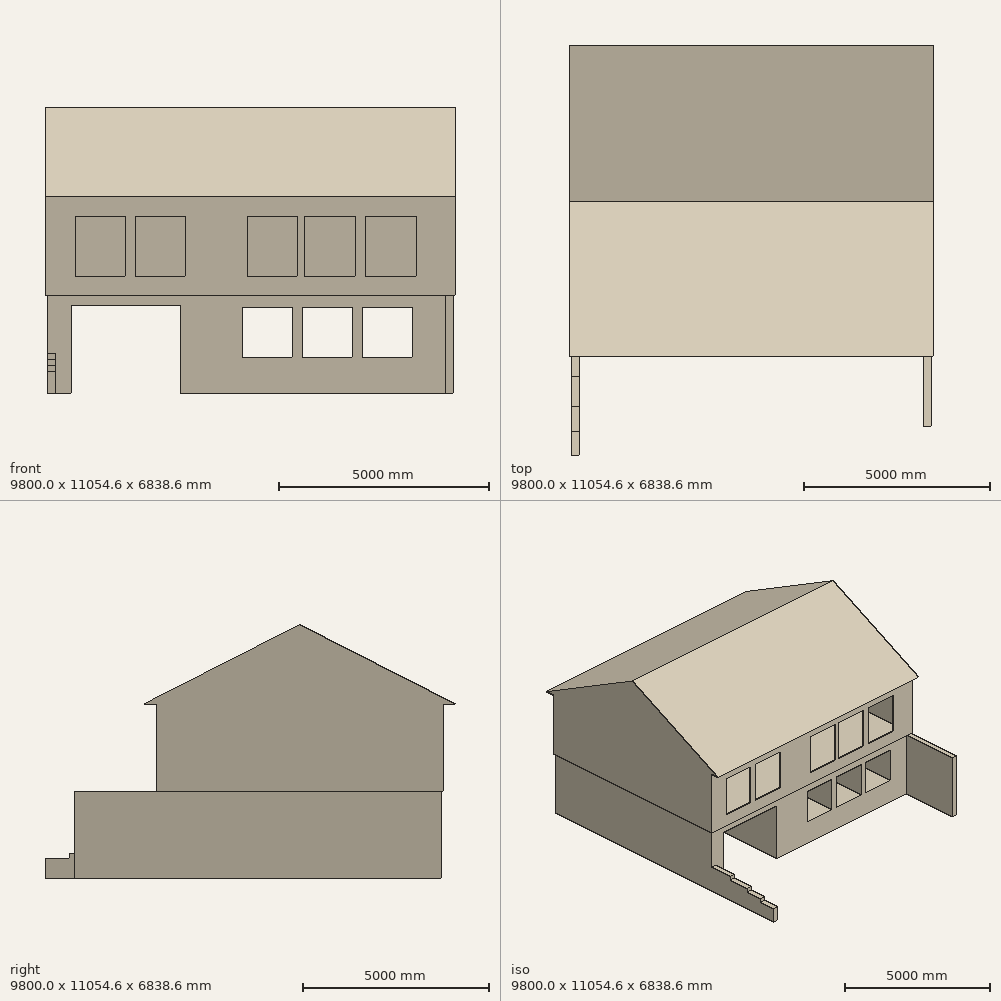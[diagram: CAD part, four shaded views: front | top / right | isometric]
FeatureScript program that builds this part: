
annotation { "Feature Type Name" : "Feature", "Feature Type Description" : "" }
export const myFeature = defineFeature(function(context is Context, id is Id, definition is map)
    precondition{}
    {
        {
            var Q0;
            Q0=qCreatedBy(makeId("Top.planeOp"),FACE);
            var sketch = newSketch(context, id + "F0", { "sketchPlane" : qUnion([Q0])});
            skLineSegment(sketch, "E0", {"start": v(-5952.09, -1613.78) * mm, "end": v(-5952.09, 1416.22) * mm});
            skLineSegment(sketch, "E1", {"start": v(-5952.09, 1416.22) * mm, "end": v(3347.91, 1416.22) * mm});
            skLineSegment(sketch, "E2", {"start": v(3347.91, 1416.22) * mm, "end": v(3347.91, -833.78) * mm});
            skLineSegment(sketch, "E3", {"start": v(3347.91, -833.78) * mm, "end": v(3547.91, -833.78) * mm});
            skLineSegment(sketch, "E4", {"start": v(3547.91, -833.78) * mm, "end": v(3547.91, 1616.22) * mm});
            skLineSegment(sketch, "E5", {"start": v(3547.91, 1616.22) * mm, "end": v(-6152.09, 1616.22) * mm});
            skLineSegment(sketch, "E6", {"start": v(-6152.09, 1616.22) * mm, "end": v(-6152.09, -1613.78) * mm});
            skLineSegment(sketch, "E7", {"start": v(-6152.09, -1613.78) * mm, "end": v(-5952.09, -1613.78) * mm});
            skLineSegment(sketch, "E8", {"start": v(-6152.09, 1616.22) * mm, "end": v(-6152.09, 9070.8) * mm});
            skLineSegment(sketch, "E9", {"start": v(-6152.09, 9070.8) * mm, "end": v(3547.91, 9070.8) * mm});
            skLineSegment(sketch, "E10", {"start": v(3547.91, 9070.8) * mm, "end": v(3547.91, 1616.22) * mm});
            skLineSegment(sketch, "E11.0", {"start": v(3347.91, 8870.8) * mm, "end": v(3347.91, 1946.22) * mm});
            skLineSegment(sketch, "E11.1", {"start": v(-5952.09, 8870.8) * mm, "end": v(3347.91, 8870.8) * mm});
            skLineSegment(sketch, "E11.2", {"start": v(-5952.09, 1946.22) * mm, "end": v(-5952.09, 8870.8) * mm});
            skSolve(sketch);
        }
        {
            var Q0;
            Q0=makeQuery(id+"F0.imprint","IMPRINT",FACE,{"disambiguationData":[TD([[makeQuery(id+"F0.imprint","IMPRINT",EDGE,{"derivedFrom":sQuery(id+"F0.wireOp",EDGE,"E0")}),1.0]])]});
            var Q1;
            {var subQ0=sQuery(id+"F0.wireOp",EDGE,"E8");Q1=makeQuery(id+"F0.imprint","IMPRINT",FACE,{"disambiguationData":[TD([[makeQuery(id+"F0.imprint","IMPRINT",EDGE,{"derivedFrom":subQ0}),-1.0]])]});}
            extrude(context, id + "F1", {"entities" : qUnion([Q0, Q1]), "depth" : 2350 * mm, "offsetDistance" : 25 * mm});
        }
        {
            var Q0;
            Q0=makeQuery(id+"F1.opExtrude","SWEPT_FACE",FACE,{"disambiguationData":[OSD([sQuery(id+"F0.wireOp",EDGE,"E0")])]});
            var sketch = newSketch(context, id + "F2", { "sketchPlane" : qUnion([Q0])});
            skLineSegment(sketch, "E12", {"start": v(-1613.78, 530) * mm, "end": v(-978.73, 530) * mm});
            skLineSegment(sketch, "E13", {"start": v(-978.73, 530) * mm, "end": v(-978.73, 670) * mm});
            skLineSegment(sketch, "E14", {"start": v(-978.73, 670) * mm, "end": v(-304.4, 670) * mm});
            skLineSegment(sketch, "E15", {"start": v(-304.4, 670) * mm, "end": v(-304.4, 810) * mm});
            skLineSegment(sketch, "E16", {"start": v(-304.4, 810) * mm, "end": v(509.11, 810) * mm});
            skLineSegment(sketch, "E17", {"start": v(509.11, 810) * mm, "end": v(509.11, 950) * mm});
            skLineSegment(sketch, "E18", {"start": v(509.11, 950) * mm, "end": v(1416.22, 950) * mm});
            skLineSegment(sketch, "E19", {"start": v(1416.22, 950) * mm, "end": v(1416.22, 2350) * mm});
            skLineSegment(sketch, "E20", {"start": v(1416.22, 2350) * mm, "end": v(-1613.78, 2350) * mm});
            skLineSegment(sketch, "E21", {"start": v(-1613.78, 2350) * mm, "end": v(-1837.63, 2350) * mm});
            skLineSegment(sketch, "E22", {"start": v(-1837.63, 2350) * mm, "end": v(-1837.63, 530) * mm});
            skLineSegment(sketch, "E23", {"start": v(-1837.63, 530) * mm, "end": v(-1613.78, 530) * mm});
            skSolve(sketch);
        }
        {
            var Q0;
            Q0=makeQuery(id+"F2.imprint","IMPRINT",FACE,{"disambiguationData":[TD([[makeQuery(id+"F2.imprint","IMPRINT",EDGE,{"derivedFrom":sQuery(id+"F2.wireOp",EDGE,"E12")}),1.0]])]});
            extrude(context, id + "F3", {"entities" : qUnion([Q0]), "operationType" : NewBodyOperationType.REMOVE, "endBound" : BoundingType.THROUGH_ALL, "oppositeDirection" : true, "depth" : 250 * mm, "offsetDistance" : 25 * mm});
        }
        {
            var Q0;
            Q0=makeQuery(id+"F3.boolean.opBoolean","MERGE",FACE,{"derivedFrom":[makeQuery(id+"F1.opExtrude","SWEPT_FACE",FACE,{"disambiguationData":[OSD([sQuery(id+"F0.wireOp",EDGE,"E1")])]})],"fromTools":[makeQuery(id+"F3.opExtrude","SWEPT_FACE",FACE,{"disambiguationData":[OSD([sQuery(id+"F2.wireOp",EDGE,"E19")])]})]});
            var sketch = newSketch(context, id + "F4", { "sketchPlane" : qUnion([Q0])});
            skLineSegment(sketch, "E24", {"start": v(-5582.09, 0) * mm, "end": v(-5582.09, 2100) * mm});
            skLineSegment(sketch, "E25", {"start": v(-5582.09, 2100) * mm, "end": v(-2982.09, 2100) * mm});
            skLineSegment(sketch, "E26", {"start": v(-2982.09, 2100) * mm, "end": v(-2982.09, 0) * mm});
            skLineSegment(sketch, "E27", {"start": v(-2982.09, 0) * mm, "end": v(-5582.09, 0) * mm});
            skLineSegment(sketch, "E28.bottom", {"start": v(1367.91, 2059.68) * mm, "end": v(2567.91, 2059.68) * mm});
            skLineSegment(sketch, "E28.top", {"start": v(1367.91, 860) * mm, "end": v(2567.91, 860) * mm});
            skLineSegment(sketch, "E28.left", {"start": v(1367.91, 2059.68) * mm, "end": v(1367.91, 860) * mm});
            skLineSegment(sketch, "E28.right", {"start": v(2567.91, 2059.68) * mm, "end": v(2567.91, 860) * mm});
            skLineSegment(sketch, "E29.1.0.0", {"start": v(-62.09, 2059.68) * mm, "end": v(-62.09, 860) * mm});
            skLineSegment(sketch, "E29.1.0.1", {"start": v(-62.09, 2059.68) * mm, "end": v(1137.91, 2059.68) * mm});
            skLineSegment(sketch, "E29.1.0.2", {"start": v(1137.91, 2059.68) * mm, "end": v(1137.91, 860) * mm});
            skLineSegment(sketch, "E29.1.0.3", {"start": v(-62.09, 860) * mm, "end": v(1137.91, 860) * mm});
            skLineSegment(sketch, "E29.2.0.0", {"start": v(-1492.09, 2059.68) * mm, "end": v(-1492.09, 860) * mm});
            skLineSegment(sketch, "E29.2.0.1", {"start": v(-1492.09, 2059.68) * mm, "end": v(-292.09, 2059.68) * mm});
            skLineSegment(sketch, "E29.2.0.2", {"start": v(-292.09, 2059.68) * mm, "end": v(-292.09, 860) * mm});
            skLineSegment(sketch, "E29.2.0.3", {"start": v(-1492.09, 860) * mm, "end": v(-292.09, 860) * mm});
            skLineSegment(sketch, "E29.direction1", {"start": v(1367.91, 860) * mm, "end": v(-62.09, 860) * mm, "construction": true});
            skSolve(sketch);
        }
        {
            var Q0;
            Q0=makeQuery(id+"F4.imprint","IMPRINT",FACE,{"disambiguationData":[TD([[makeQuery(id+"F4.imprint","IMPRINT",EDGE,{"derivedFrom":sQuery(id+"F4.wireOp",EDGE,"E24")}),-1.0]])]});
            var Q1;
            Q1=makeQuery(id+"F4.imprint","IMPRINT",FACE,{"disambiguationData":[TD([[makeQuery(id+"F4.imprint","IMPRINT",EDGE,{"derivedFrom":sQuery(id+"F4.wireOp",EDGE,"E29.2.0.0")}),1.0]])]});
            var Q2;
            Q2=makeQuery(id+"F4.imprint","IMPRINT",FACE,{"disambiguationData":[TD([[makeQuery(id+"F4.imprint","IMPRINT",EDGE,{"derivedFrom":sQuery(id+"F4.wireOp",EDGE,"E29.1.0.0")}),1.0]])]});
            var Q3;
            Q3=makeQuery(id+"F4.imprint","IMPRINT",FACE,{"disambiguationData":[TD([[makeQuery(id+"F4.imprint","IMPRINT",EDGE,{"derivedFrom":sQuery(id+"F4.wireOp",EDGE,"E28.bottom")}),-1.0]])]});
            extrude(context, id + "F5", {"entities" : qUnion([Q0, Q1, Q2, Q3]), "operationType" : NewBodyOperationType.REMOVE, "endBound" : BoundingType.UP_TO_NEXT, "oppositeDirection" : true, "depth" : 25 * mm, "offsetDistance" : 25 * mm});
        }
        {
            var Q0;
            Q0=makeQuery(id+"F1.opExtrude","CAP_FACE",FACE,{"disambiguationData":[OSD([sQuery(id+"F0.wireOp",EDGE,"E0"),sQuery(id+"F0.wireOp",EDGE,"E1"),sQuery(id+"F0.wireOp",EDGE,"E2"),sQuery(id+"F0.wireOp",EDGE,"E3"),sQuery(id+"F0.wireOp",EDGE,"E4"),sQuery(id+"F0.wireOp",EDGE,"E5"),sQuery(id+"F0.wireOp",EDGE,"E6"),sQuery(id+"F0.wireOp",EDGE,"E7"),sQuery(id+"F0.wireOp",EDGE,"E8"),sQuery(id+"F0.wireOp",EDGE,"E9"),sQuery(id+"F0.wireOp",EDGE,"E10"),sQuery(id+"F0.wireOp",EDGE,"E11.0"),sQuery(id+"F0.wireOp",EDGE,"E11.1"),sQuery(id+"F0.wireOp",EDGE,"E11.2")])],"isStart":false});
            var sketch = newSketch(context, id + "F6", { "sketchPlane" : qUnion([Q0])});
            skLineSegment(sketch, "E30.bottom", {"start": v(-6152.09, 9070.8) * mm, "end": v(3547.91, 9070.8) * mm});
            skLineSegment(sketch, "E30.top", {"start": v(-6152.09, 1416.22) * mm, "end": v(3547.91, 1416.22) * mm});
            skLineSegment(sketch, "E30.left", {"start": v(-6152.09, 9070.8) * mm, "end": v(-6152.09, 1416.22) * mm});
            skLineSegment(sketch, "E30.right", {"start": v(3547.91, 9070.8) * mm, "end": v(3547.91, 1416.22) * mm});
            skLineSegment(sketch, "E31.0", {"start": v(-6202.09, 9120.8) * mm, "end": v(-6202.09, 1366.22) * mm});
            skLineSegment(sketch, "E31.1", {"start": v(-6202.09, 9120.8) * mm, "end": v(3597.91, 9120.8) * mm});
            skLineSegment(sketch, "E31.2", {"start": v(3597.91, 9120.8) * mm, "end": v(3597.91, 1366.22) * mm});
            skLineSegment(sketch, "E31.3", {"start": v(-6202.09, 1366.22) * mm, "end": v(3597.91, 1366.22) * mm});
            skSolve(sketch);
        }
        {
            var Q0;
            Q0=makeQuery(id+"F6.imprint","IMPRINT",FACE,{"disambiguationData":[TD([[makeQuery(id+"F6.imprint","IMPRINT",EDGE,{"derivedFrom":sQuery(id+"F6.wireOp",EDGE,"E30.bottom")}),1.0]])]});
            var Q1;
            {var subQ0=sQuery(id+"F6.wireOp",EDGE,"E30.top");var subQ1=makeQuery(id+"F1.opExtrude","CAP_EDGE",EDGE,{"disambiguationData":[OSD([sQuery(id+"F0.wireOp",EDGE,"E2")])],"isStart":false});var subQ2=makeQuery(id+"F6.imprint","INTERSECT",VERTEX,{"derivedFrom":[subQ1,subQ0]});Q1=makeQuery(id+"F6.imprint","IMPRINT",FACE,{"disambiguationData":[TD([[makeQuery(id+"F6.imprint","IMPRINT",EDGE,{"disambiguationData":[TD([[subQ2,-1.0]])],"derivedFrom":subQ1}),1.0]])]});}
            extrude(context, id + "F7", {"entities" : qUnion([Q0, Q1]), "depth" : 2350 * mm, "offsetDistance" : 25 * mm});
        }
        {
            var Q0;
            Q0=makeQuery(id+"F7.opExtrude","SWEPT_FACE",FACE,{"disambiguationData":[OSD([sQuery(id+"F6.wireOp",EDGE,"E31.3")])]});
            var sketch = newSketch(context, id + "F8", { "sketchPlane" : qUnion([Q0])});
            skLineSegment(sketch, "E32.bottom", {"start": v(-5495.4, 4220.4) * mm, "end": v(-4289.93, 4220.4) * mm});
            skLineSegment(sketch, "E32.top", {"start": v(-5495.4, 2795.64) * mm, "end": v(-4289.93, 2795.64) * mm});
            skLineSegment(sketch, "E32.left", {"start": v(-5495.4, 4220.4) * mm, "end": v(-5495.4, 2795.64) * mm});
            skLineSegment(sketch, "E32.right", {"start": v(-4289.93, 4220.4) * mm, "end": v(-4289.93, 2795.64) * mm});
            skPoint(sketch, "E33.firstSnap0", {"position": v(-4892.66, 4220.4) * mm});
            skLineSegment(sketch, "E33.bottom", {"start": v(-4055.7, 4220.4) * mm, "end": v(-2854.53, 4220.4) * mm});
            skLineSegment(sketch, "E33.top", {"start": v(-4055.7, 2795.64) * mm, "end": v(-2854.53, 2795.64) * mm});
            skLineSegment(sketch, "E33.left", {"start": v(-4055.7, 4220.4) * mm, "end": v(-4055.7, 2795.64) * mm});
            skLineSegment(sketch, "E33.right", {"start": v(-2854.53, 4220.4) * mm, "end": v(-2854.53, 2795.64) * mm});
            skPoint(sketch, "E34.firstSnap0", {"position": v(-3455.1, 4220.4) * mm});
            skLineSegment(sketch, "E34.bottom", {"start": v(-1382.96, 4220.4) * mm, "end": v(-181.8, 4220.4) * mm});
            skLineSegment(sketch, "E34.top", {"start": v(-1382.96, 2795.64) * mm, "end": v(-181.8, 2795.64) * mm});
            skLineSegment(sketch, "E34.left", {"start": v(-1382.96, 4220.4) * mm, "end": v(-1382.96, 2795.64) * mm});
            skLineSegment(sketch, "E34.right", {"start": v(-181.8, 4220.4) * mm, "end": v(-181.8, 2795.64) * mm});
            skLineSegment(sketch, "E35.bottom", {"start": v(0, 2795.64) * mm, "end": v(1206.57, 2795.64) * mm});
            skLineSegment(sketch, "E35.top", {"start": v(0, 4220.4) * mm, "end": v(1206.57, 4220.4) * mm});
            skLineSegment(sketch, "E35.left", {"start": v(0, 2795.64) * mm, "end": v(0, 4220.4) * mm});
            skLineSegment(sketch, "E35.right", {"start": v(1206.57, 2795.64) * mm, "end": v(1206.57, 4220.4) * mm});
            skLineSegment(sketch, "E36.bottom", {"start": v(1445.76, 4220.4) * mm, "end": v(2669, 4220.4) * mm});
            skLineSegment(sketch, "E36.top", {"start": v(1445.76, 2795.64) * mm, "end": v(2669, 2795.64) * mm});
            skLineSegment(sketch, "E36.left", {"start": v(1445.76, 4220.4) * mm, "end": v(1445.76, 2795.64) * mm});
            skLineSegment(sketch, "E36.right", {"start": v(2669, 4220.4) * mm, "end": v(2669, 2795.64) * mm});
            skSolve(sketch);
        }
        {
            var Q0;
            Q0 = qSketchRegion(id + "F8", true);
            extrude(context, id + "F9", {"entities" : qUnion([Q0]), "operationType" : NewBodyOperationType.REMOVE, "endBound" : BoundingType.UP_TO_NEXT, "oppositeDirection" : true, "depth" : 25 * mm, "offsetDistance" : 25 * mm});
        }
        {
            var Q0;
            Q0=makeQuery(id+"F7.opExtrude","SWEPT_FACE",FACE,{"disambiguationData":[OSD([sQuery(id+"F6.wireOp",EDGE,"E31.0")])]});
            var sketch = newSketch(context, id + "F10", { "sketchPlane" : qUnion([Q0])});
            skLineSegment(sketch, "E37", {"start": v(-9440.8, 4700) * mm, "end": v(-5243.5, 6838.62) * mm});
            skLineSegment(sketch, "E38", {"start": v(-5243.5, 6838.62) * mm, "end": v(-1046.22, 4700) * mm});
            skLineSegment(sketch, "E39", {"start": v(-1046.22, 4700) * mm, "end": v(-9440.8, 4700) * mm});
            skSolve(sketch);
        }
        {
            var Q0;
            {var subQ5=sQuery(id+"F10.wireOp",EDGE,"E37");Q0=makeQuery(id+"F10.imprint","IMPRINT",FACE,{"disambiguationData":[TD([[makeQuery(id+"F10.imprint","IMPRINT",EDGE,{"derivedFrom":subQ5}),-1.0]])]});}
            var Q1;
            Q1=makeQuery(id+"F7.opExtrude","SWEPT_FACE",FACE,{"disambiguationData":[OSD([sQuery(id+"F6.wireOp",EDGE,"E31.2")])]});
            extrude(context, id + "F11", {"entities" : qUnion([Q0]), "operationType" : NewBodyOperationType.ADD, "endBound" : BoundingType.UP_TO_SURFACE, "oppositeDirection" : true, "depth" : 11025 * mm, "endBoundEntityFace" : qUnion([Q1]), "offsetDistance" : 25 * mm});
        }
    });
